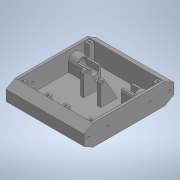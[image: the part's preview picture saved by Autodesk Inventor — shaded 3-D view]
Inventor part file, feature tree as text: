
AUTODESK INVENTOR PART (.ipt)
format: ipt  version: 2020 (Build 240168000, 168)  size: 375,296 bytes
history: native  units: in
note: dims shown in document units (in); Inventor stores cm internally (conversion verified against a paired STEP export)
features: projected_geometry x13, extrude x11, sketch x11, mirror x4, plane x1
ambient origin geometry x8: Origin, YZ Plane, XZ Plane, XY Plane, X Axis, Y Axis, Z Axis, Center Point
bodies: Solid1 (feature_tree)
feature tree (40):
  extrude  "Extrusion1"  Depth=5.9055in
  extrude  "Extrusion2"  TaperAngle=0.0deg  [1 undecoded]
  extrude  "Extrusion3"  Depth=1.2598in
  extrude  "Extrusion4"  Depth=0.315in
  extrude  "Extrusion5"  TaperAngle=0.0deg  [1 undecoded]
  extrude  "Extrusion6"  Depth=0.689in
  mirror  "Mirror1"
  extrude  "Extrusion7"  Depth=0.0787in
  mirror  "Mirror2"
  extrude  "Extrusion8"  Depth=0.5512in
  mirror  "Mirror3"
  plane  "Work Plane1"
  extrude  "Extrusion9"  Depth=0.7874in TaperAngle=0.0deg
  mirror  "Mirror4"
  extrude  "Extrusion10"  Depth=6.063in TaperAngle=0.0deg
  extrude  "Extrusion11"  Depth=0.1575in
  sketch  "Sketch1"  dims[d0=1.378in d1=5.9055in]
  sketch  "Sketch2"  dims[d2=5.1181in d3=0.0in]
  projected_geometry  "Projected Loop1"
  sketch  "Sketch3"  dims[d4=0.1575in d5=1.2598in]
  projected_geometry  "Projected Loop2"
  projected_geometry  "Projected Loop3"
  sketch  "Sketch4"  dims[d6=0.0in d8=0.315in]
  sketch  "Sketch5"  dims[d10=1.1898in d11=0.0in]
  projected_geometry  "Projected Loop4"
  sketch  "Sketch6"  dims[d12=0.6496in d13=0.689in]
  sketch  "Sketch7"  dims[d14=1.5748in d15=0.0787in]
  sketch  "Sketch9"  dims[d16=0.5512in d17=0.0in d18=0.6102in]
  sketch  "Sketch10"  dims[d19=0.4803in d20=0.7874in d21=0.0in]
  sketch  "Sketch12"  dims[d22=0.1654in d23=6.063in d24=0.0in]
  projected_geometry  "Projected Loop6"
  projected_geometry  "Projected Loop7"
  projected_geometry  "Projected Loop8"
  sketch  "Sketch13"  dims[d25=0.5967in d26=0.1575in d27=1.5748in d28=0.0in d29=0.0in d30=0.1575in d31=0.2756in d32=0.0in d33=0.4331in d34=0.122in d38=2.7559in d40=0.061in d41=0.0787in d42=0.2362in d43=0.0in d44=60.0deg d45=0.0787in d46=0.315in d48=1.1898in d49=0.0in d51=0.1575in d52=0.1575in d53=0.2756in d54=0.0in]
  projected_geometry  "Projected Loop9"
  projected_geometry  "Projected Loop10"
  projected_geometry  "Projected Loop11"
  projected_geometry  "Projected Loop12"
  projected_geometry  "Projected Loop13"
  projected_geometry  "Projected Loop14"
note: 2 required parameter values undecoded (feature->parameter linkage not recoverable at this tier; creation-order binding heuristic only, values carry confidence <= 0.55)
